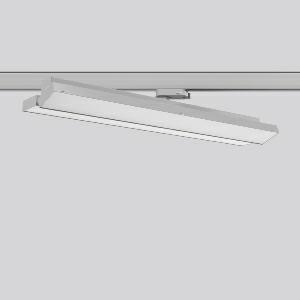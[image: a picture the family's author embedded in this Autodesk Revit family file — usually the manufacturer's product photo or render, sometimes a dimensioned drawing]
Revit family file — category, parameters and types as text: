
# Revit family: tx-move_742164_004_3_76_7f7c
name_source: partatom
category: Lighting Fixtures
units: mm (PartAtom-declared; Revit-internal decimal feet)

## family parameters
Cut with Voids When Loaded = No
Host = Face
Light Source = No
Part Type = Normal
Room Calculation Point = No
Round Connector Dimension = Use Diameter
Shared = No

## types (1)
- MultiLumen 1 (1 x LED Modul 835, 2550 lm, 3500)
    Apparent Load = 41 VA
    CIE Flux Codes = 47 79 96 100 100
    Color Rendering = 80
    Color Temperature = 3500
    Default Elevation = 1800 mm
    Description = Series: TX-MOVE
Multifunctional surface-mounted spotlight for area lighting. Very flat design. Housing: sheet steel, powder-coated. Rotation range: 356°. Swivel range: 90°. Consistent alignment possible with visible tilt scale. High-efficiency LED units with flush-mounted opal diffuser made of non-yellowing PMMA. Symmetrical wide beam light emission. With adapter for RZB 3-circuit DALI tracks. Suitable for Track on ceiling. MultiLumen: Luminous flux adjustable in 3 steps. Factory setting is the highest luminous flux. Environmentally friendly and resource-saving due to replaceable and recyclable components. 
Colour: silver, matt (approx. RAL 9006)
Length: 570 mm
Width: 119 mm
Height: 88 mm
Lamp: LED
Socket: without socket
Colour temperature: 3500K
Colour rendering index (CRI): 80
System power: 41 W
Rated luminous flux: 5100 lm
Luminous efficiency: 124 lm/W
System power 2: 57 W
Rated luminous flux 2: 6950 lm
Luminous efficiency 2: 122 lm/W
System power 3: 73 W
Rated luminous flux 3: 8500 lm
Luminous efficiency 3: 116 lm/W
Control gear: Dimmable EVG, DALI
Protection class: I
Type of protection: IP 20
    Height = 75 mm
    Lamp = 1 x LED Modul 835
    Lamp Light Flux = 2550 lm
    Lamp count = 1
    Length = 569 mm
    Lifetime = 50000 h
    Luminous efficacy = 124 lm/W
    Manufacturer = RZB
    ModVariant = No
    Model = 742164.004.3.76
    Mounting Place = Ceiling
    Mounting Type = Rail mounted
    Number of Poles = 1
    OnlyDefault = Yes
    Power Factor = 1
    Product Name = TX-MOVE
    Product group = Track mounted projectors
    ProductGroupID = 301
    Protection Class = Protection class I
    Protection Degree = IP 20
    RLX_Detail_Level = 1
    RLX_Emergency_Light_Flux = 0 lm
    RLX_Emergency_Type = 0
    RLX_Emergency_Type_DB = No
    RlxData = <blob elided: 32329 chars, md5=2f872345>
    Socket = socket
    Standby Power = 0 W
    System Light Flux = 5100 lm
    System Power = 41 W
    Type Comments = MultiLumen 1
    Type Image = 742164.004.jpg
    URL = http://relux.com
    VarID = multilumen_1
    Voltage = 230 V
    Voltage Range = 220-240 V
    Weight = 0.00 kg
    Width = 119 mm

## geometry (parser evidence)
native form markers: Blend x4, Sweep x13
no freeform markers — native parametric forms only
